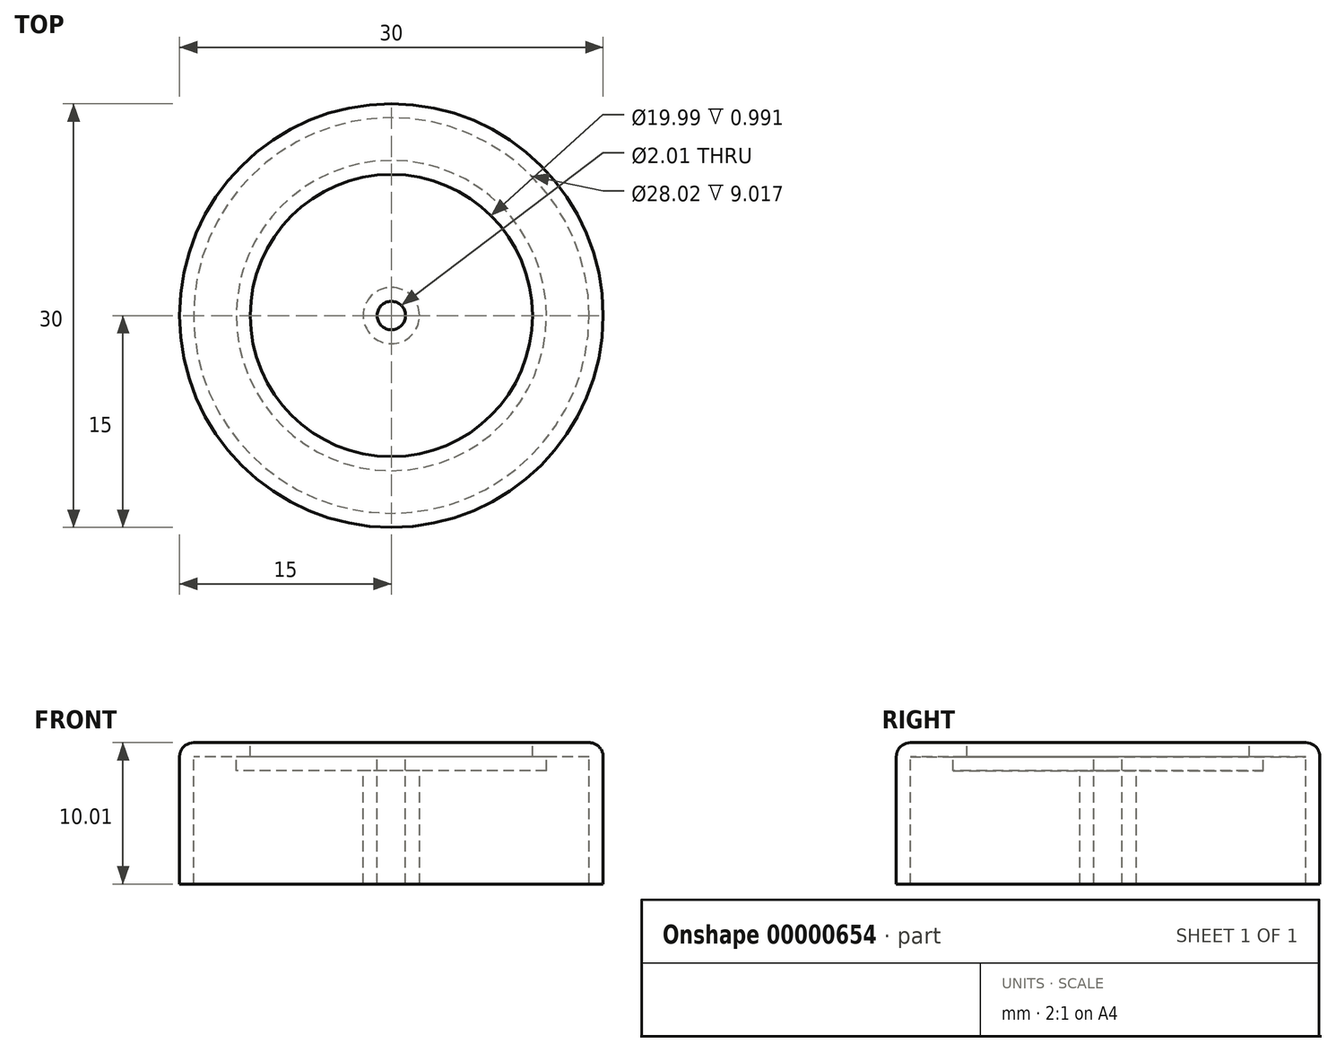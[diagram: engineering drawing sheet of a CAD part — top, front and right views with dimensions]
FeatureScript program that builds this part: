
annotation { "Feature Type Name" : "Feature", "Feature Type Description" : "" }
export const myFeature = defineFeature(function(context is Context, id is Id, definition is map)
    precondition{}
    {
        {
            var Q0;
            Q0=qCreatedBy(makeId("Top.planeOp"),FACE);
            var sketch = newSketch(context, id + "F0", { "sketchPlane" : qUnion([Q0])});
            skCircle(sketch, "E0", {"center": v(0, 0) * mm, "radius": 15 * mm});
            skSolve(sketch);
        }
        {
            var Q0;
            Q0=makeQuery(id+"F0.imprint","IMPRINT",FACE,{"disambiguationData":[TD([[makeQuery(id+"F0.imprint","IMPRINT",EDGE,{"derivedFrom":sQuery(id+"F0.wireOp",EDGE,"E0")}),1.0]])]});
            var Q1;
            Q1=sQuery(id+"F0.wireOp",EDGE,"E0");
            extrude(context, id + "F1", {"entities" : qUnion([Q0]), "surfaceEntities" : qUnion([Q1]), "oppositeDirection" : true, "depth" : 10 * mm});
        }
        {
            var Q0;
            Q0=makeQuery(id+"F1.opExtrude","CAP_FACE",FACE,{"disambiguationData":[OSD([sQuery(id+"F0.wireOp",EDGE,"E0")])],"isStart":true});
            var sketch = newSketch(context, id + "F2", { "sketchPlane" : qUnion([Q0])});
            skCircle(sketch, "E1", {"center": v(0, 0) * mm, "radius": 10 * mm});
            skSolve(sketch);
        }
        {
            var Q0;
            Q0 = qSketchRegion(id + "F2", true);
            extrude(context, id + "F3", {"entities" : qUnion([Q0]), "operationType" : NewBodyOperationType.REMOVE, "oppositeDirection" : true, "depth" : 1 * mm});
        }
        {
            var Q0;
            Q0=qCreatedBy(makeId("Top.planeOp"),FACE);
            var sketch = newSketch(context, id + "F4", { "sketchPlane" : qUnion([Q0])});
            skCircle(sketch, "E2", {"center": v(0, 0) * mm, "radius": 1 * mm});
            skSolve(sketch);
        }
        {
            var Q0;
            Q0 = qSketchRegion(id + "F4", true);
            extrude(context, id + "F5", {"entities" : qUnion([Q0]), "operationType" : NewBodyOperationType.REMOVE, "endBound" : BoundingType.THROUGH_ALL, "oppositeDirection" : true, "depth" : 25.4 * mm});
        }
        {
            var Q0;
            Q0=makeQuery(id+"F1.opExtrude","CAP_EDGE",EDGE,{"disambiguationData":[OSD([sQuery(id+"F0.wireOp",EDGE,"E0")])],"isStart":true});
            fillet(context, id + "F6", {"entities" : qUnion([Q0]), "radius" : 1 * mm, "tangentPropagation" : true, "allowEdgeOverflow" : false});
        }
        {
            var Q0;
            Q0=makeQuery(id+"F1.opExtrude","CAP_FACE",FACE,{"disambiguationData":[OSD([sQuery(id+"F0.wireOp",EDGE,"E0")])],"isStart":false});
            shell(context, id + "F7", {"entities" : qUnion([Q0]), "thickness" : 1 * mm});
        }
    });
